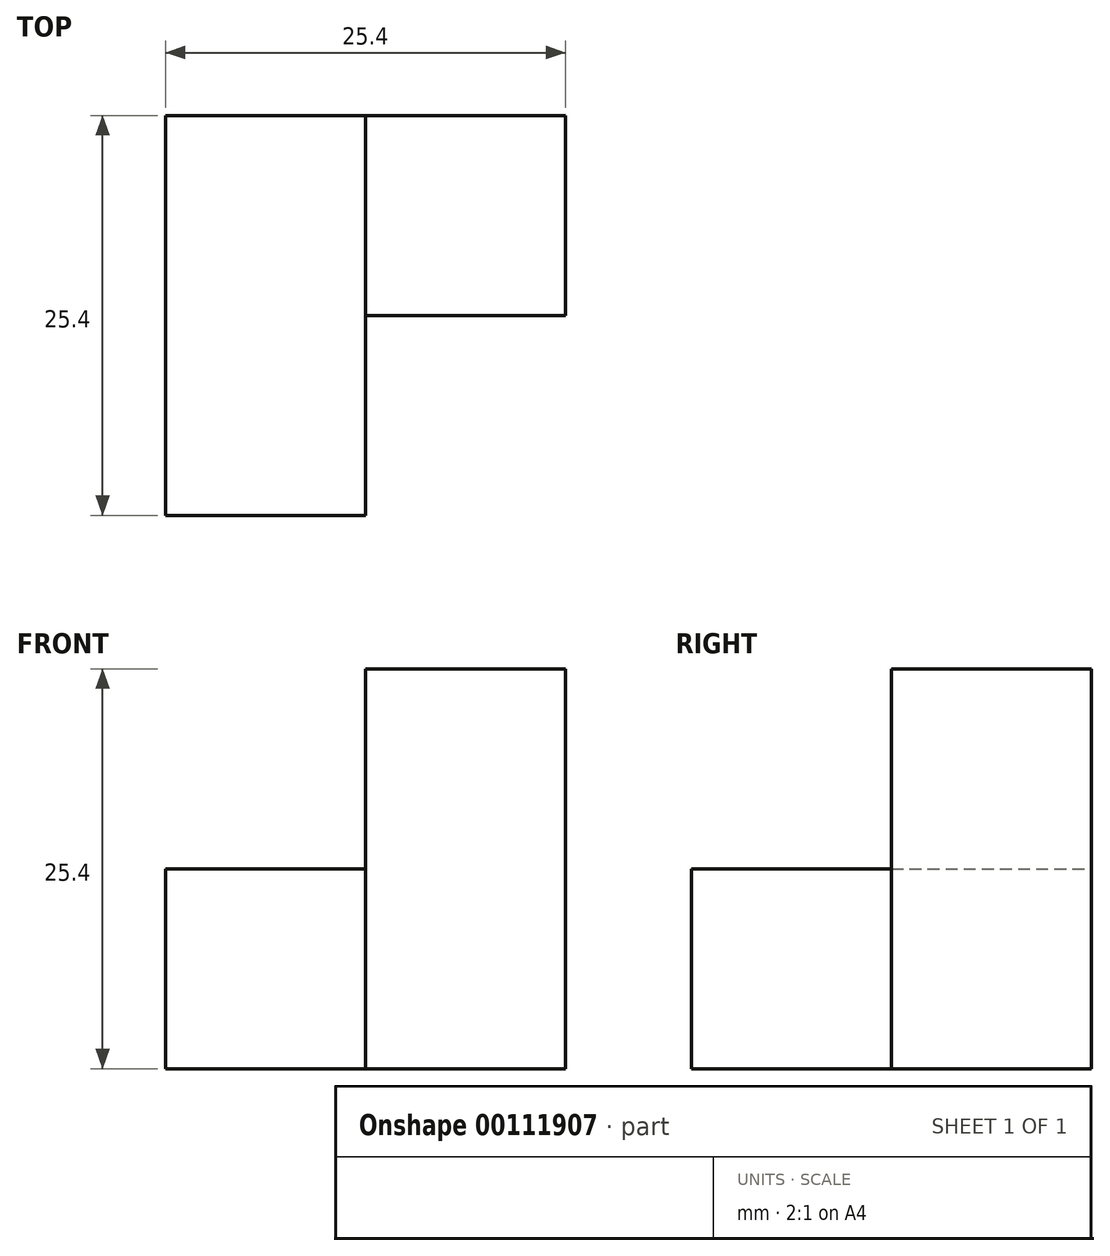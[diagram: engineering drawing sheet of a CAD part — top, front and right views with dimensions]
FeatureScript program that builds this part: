
annotation { "Feature Type Name" : "Feature", "Feature Type Description" : "" }
export const myFeature = defineFeature(function(context is Context, id is Id, definition is map)
    precondition{}
    {
        {
            var Q0;
            Q0=qCreatedBy(makeId("Front.planeOp"),FACE);
            var sketch = newSketch(context, id + "F0", { "sketchPlane" : qUnion([Q0])});
            skLineSegment(sketch, "E0.bottom", {"start": v(-15.08, 14.29) * mm, "end": v(-2.38, 14.29) * mm});
            skLineSegment(sketch, "E0.top", {"start": v(-15.08, 1.59) * mm, "end": v(-2.38, 1.59) * mm});
            skLineSegment(sketch, "E0.left", {"start": v(-15.08, 14.29) * mm, "end": v(-15.08, 1.59) * mm});
            skLineSegment(sketch, "E0.right", {"start": v(-2.38, 14.29) * mm, "end": v(-2.38, 1.59) * mm});
            skSolve(sketch);
        }
        {
            var Q0;
            Q0 = qSketchRegion(id + "F0", true);
            extrude(context, id + "F1", {"entities" : qUnion([Q0]), "depth" : 12.7 * mm});
        }
        {
            var Q0;
            Q0=makeQuery(id+"F1.opExtrude","CAP_FACE",FACE,{"disambiguationData":[OSD([sQuery(id+"F0.wireOp",EDGE,"E0.bottom"),sQuery(id+"F0.wireOp",EDGE,"E0.top"),sQuery(id+"F0.wireOp",EDGE,"E0.left"),sQuery(id+"F0.wireOp",EDGE,"E0.right")])],"isStart":false});
            extrude(context, id + "F2", {"entities" : qUnion([Q0]), "operationType" : NewBodyOperationType.ADD, "depth" : 12.7 * mm});
        }
        {
            var Q0;
            {var subQ0=sQuery(id+"F0.wireOp",EDGE,"E0.right");Q0=makeQuery(id+"F2.boolean.opBoolean","MERGE",FACE,{"derivedFrom":[makeQuery(id+"F1.opExtrude","SWEPT_FACE",FACE,{"disambiguationData":[OSD([subQ0])]}),makeQuery(id+"F2.opExtrude","SWEPT_FACE",FACE,{"disambiguationData":[OSD([subQ0])]})]});}
            var sketch = newSketch(context, id + "F3", { "sketchPlane" : qUnion([Q0])});
            skLineSegment(sketch, "E1", {"start": v(-12.7, 14.29) * mm, "end": v(-12.7, 1.59) * mm});
            skSolve(sketch);
        }
        {
            var Q0;
            Q0 = qSketchRegion(id + "F3", true);
            var Q1;
            {var subQ0=sQuery(id+"F3.wireOp",EDGE,"E1");Q1=makeQuery(id+"F3.imprint","IMPRINT",FACE,{"disambiguationData":[TD([[makeQuery(id+"F3.imprint","IMPRINT",EDGE,{"derivedFrom":subQ0}),1.0]])]});}
            extrude(context, id + "F4", {"entities" : qUnion([Q0, Q1]), "operationType" : NewBodyOperationType.ADD, "depth" : 12.7 * mm});
        }
        {
            var Q0;
            {var subQ0=sQuery(id+"F0.wireOp",EDGE,"E0.bottom");Q0=makeQuery(id+"F4.boolean.opBoolean","MERGE",FACE,{"derivedFrom":[makeQuery(id+"F2.boolean.opBoolean","MERGE",FACE,{"derivedFrom":[makeQuery(id+"F1.opExtrude","SWEPT_FACE",FACE,{"disambiguationData":[OSD([subQ0])]}),makeQuery(id+"F2.opExtrude","SWEPT_FACE",FACE,{"disambiguationData":[OSD([subQ0])]})]}),makeQuery(id+"F4.opExtrude","SWEPT_FACE",FACE,{"disambiguationData":[OSD([subQ0,sQuery(id+"F0.wireOp",EDGE,"E0.right")])]})]});}
            var sketch = newSketch(context, id + "F5", { "sketchPlane" : qUnion([Q0])});
            skLineSegment(sketch, "E2", {"start": v(-2.38, -12.7) * mm, "end": v(-2.38, 0) * mm});
            skSolve(sketch);
        }
        {
            var Q0;
            Q0 = qSketchRegion(id + "F5", true);
            var Q1;
            {var subQ0=sQuery(id+"F5.wireOp",EDGE,"E2");Q1=makeQuery(id+"F5.imprint","IMPRINT",FACE,{"disambiguationData":[TD([[makeQuery(id+"F5.imprint","IMPRINT",EDGE,{"derivedFrom":subQ0}),-1.0]])]});}
            extrude(context, id + "F6", {"entities" : qUnion([Q0, Q1]), "operationType" : NewBodyOperationType.ADD, "depth" : 12.7 * mm});
        }
    });
